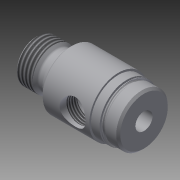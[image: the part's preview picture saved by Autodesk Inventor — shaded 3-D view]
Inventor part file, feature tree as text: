
AUTODESK INVENTOR PART (.ipt)
format: ipt  version: 2014 SP2 (Build 180246200, 246)  size: 272,896 bytes
history: native  units: in
note: dims shown in document units (in); Inventor stores cm internally (conversion verified against a paired STEP export)
features: other x119, sketch x6, revolve x5, thread x2, hole x1
ambient origin geometry x8: Origin, YZ Plane, XZ Plane, XY Plane, X Axis, Y Axis, Z Axis, Center Point
bodies: Solid1 (feature_tree)
feature tree (133):
  revolve  "Revolution1"  [1 undecoded]
  thread  "Thread1"  [1 undecoded]
  revolve  "Revolution2"  Angle=360.0deg
  hole  "Hole1"  [1 undecoded]
  revolve  "Revolution3"  [1 undecoded]
  revolve  "Revolution4"  [1 undecoded]
  thread  "Thread2"  [1 undecoded]
  revolve  "Revolution5"  [1 undecoded]
  other  "dp1_XY"
  other  "dp1_YZ"
  other  "dp1_ZX"
  other  "dp1_X"
  other  "dp1_Y"
  other  "dp1_Z"
  other  "dp1_Center"
  other  "dp2_XY"
  other  "dp2_YZ"
  other  "dp2_ZX"
  other  "dp2_X"
  other  "dp2_Y"
  other  "dp2_Z"
  other  "dp2_Center"
  other  "hh_XY"
  other  "hh_YZ"
  other  "hh_ZX"
  other  "hh_X"
  other  "hh_Y"
  other  "hh_Z"
  other  "hh_Center"
  other  "port_XY"
  other  "port_YZ"
  other  "port_ZX"
  other  "port_X"
  other  "port_Y"
  other  "port_Z"
  other  "port_Center"
  other  "rod_guide_XY"
  other  "rod_guide_YZ"
  other  "rod_guide_ZX"
  other  "rod_guide_X"
  other  "rod_guide_Y"
  other  "rod_guide_Z"
  other  "rod_guide_Center"
  other  "s1_XY"
  other  "s1_YZ"
  other  "s1_ZX"
  other  "s1_X"
  other  "s1_Y"
  other  "s1_Z"
  other  "s1_Center"
  other  "s2_XY"
  other  "s2_YZ"
  other  "s2_ZX"
  other  "s2_X"
  other  "s2_Y"
  other  "s2_Z"
  other  "s2_Center"
  other  "t1_XY"
  other  "t1_YZ"
  other  "t1_ZX"
  other  "t1_X"
  other  "t1_Y"
  other  "t1_Z"
  other  "t1_Center"
  other  "t111_XY"
  other  "t111_YZ"
  other  "t111_ZX"
  other  "t111_X"
  other  "t111_Y"
  other  "t111_Z"
  other  "t111_Center"
  other  "to_foot_bracket_XY"
  other  "to_foot_bracket_YZ"
  other  "to_foot_bracket_ZX"
  other  "to_foot_bracket_X"
  other  "to_foot_bracket_Y"
  other  "to_foot_bracket_Z"
  other  "to_foot_bracket_Center"
  other  "to_nut_XY"
  other  "to_nut_YZ"
  other  "to_nut_ZX"
  other  "to_nut_X"
  other  "to_nut_Y"
  other  "to_nut_Z"
  other  "to_nut_Center"
  other  "to_rod_XY"
  other  "to_rod_YZ"
  other  "to_rod_ZX"
  other  "to_rod_X"
  other  "to_rod_Y"
  other  "to_rod_Z"
  other  "to_rod_Center"
  other  "to_screw_XY"
  other  "to_screw_YZ"
  other  "to_screw_ZX"
  other  "to_screw_X"
  other  "to_screw_Y"
  other  "to_screw_Z"
  other  "to_screw_Center"
  other  "to_trunnion_brackets_XY"
  other  "to_trunnion_brackets_YZ"
  other  "to_trunnion_brackets_ZX"
  other  "to_trunnion_brackets_X"
  other  "to_trunnion_brackets_Y"
  other  "to_trunnion_brackets_Z"
  other  "to_trunnion_brackets_Center"
  other  "to_trunnion_brackets1_XY"
  other  "to_trunnion_brackets1_YZ"
  other  "to_trunnion_brackets1_ZX"
  other  "to_trunnion_brackets1_X"
  other  "to_trunnion_brackets1_Y"
  other  "to_trunnion_brackets1_Z"
  other  "to_trunnion_brackets1_Center"
  other  "to_trunnion_brackets2_XY"
  other  "to_trunnion_brackets2_YZ"
  other  "to_trunnion_brackets2_ZX"
  other  "to_trunnion_brackets2_X"
  other  "to_trunnion_brackets2_Y"
  other  "to_trunnion_brackets2_Z"
  other  "to_trunnion_brackets2_Center"
  other  "to_tube_XY"
  other  "to_tube_YZ"
  other  "to_tube_ZX"
  other  "to_tube_X"
  other  "to_tube_Y"
  other  "to_tube_Z"
  other  "to_tube_Center"
  sketch  "Sketch_2"  dims[d0=360.0deg d1=0.23in d2=0.0in d3=360.0deg]
  sketch  "Sketch_3"  dims[d4=0.2535in d5=0.75in d6=0.2735in d7=0.25in d8=90.0deg d9=1.594in d10=0.0in d11=360.0deg]
  sketch  "Sketch3"  dims[d12=360.0deg d13=0.1501in d14=0.0in]
  sketch  "Sketch_10"  dims[d15=360.0deg]
  sketch  "Sketch_40"  dims[d16=0.0in d17=0.0in d18=0.0in d19=0.0in d20=0.0in]
  sketch  "Sketch_47"
note: 7 required parameter values undecoded (feature->parameter linkage not recoverable at this tier; creation-order binding heuristic only, values carry confidence <= 0.55)